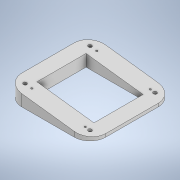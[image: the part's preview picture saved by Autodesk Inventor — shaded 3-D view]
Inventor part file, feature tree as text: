
AUTODESK INVENTOR PART (.ipt)
format: ipt  version: 2021 (Build 250183000, 183)  size: 180,224 bytes
history: native  units: mm
features: sketch x8, extrude x3, hole x3, projected_geometry x3, other x2, plane x2, fillet x1
ambient origin geometry x8: Origin, YZ Plane, XZ Plane, XY Plane, X Axis, Y Axis, Z Axis, Center Point
bodies: Body1 (feature_tree)
feature tree (22):
  other  "實體1"
  extrude  "擠出1"  Depth=265.0mm
  extrude  "擠出2"  Depth=265.0mm
  sketch  "草圖4"
  plane  "工作平面2"
  other  "分割1"
  hole  "孔1"  [1 undecoded]
  hole  "孔2"  [1 undecoded]
  hole  "孔3"  [1 undecoded]
  extrude  "擠出3"  Depth=10.0mm
  fillet  "圓角1"  Radius=1.22173mm
  plane  "工作平面1"
  sketch  "草圖2"
  sketch  "草圖1"
  projected_geometry  "投影迴路1"
  sketch  "草圖3"
  projected_geometry  "投影迴路2"
  projected_geometry  "投影迴路3"
  sketch  "草圖5"
  sketch  "草圖6"
  sketch  "草圖7"
  sketch  "草圖8"
note: 3 required parameter values undecoded (feature->parameter linkage not recoverable at this tier; creation-order binding heuristic only, values carry confidence <= 0.55)
